# Revit family: Island_LivingDivaniBIM
name_source: partatom
category: Arredi
revit_build: Autodesk Revit 2017 (Build: 20190508_0315(x64)
units: mm (PartAtom-declared; Revit-internal decimal feet)

## family parameters
Basato su piano di lavoro = No
Condiviso = No
Numero OmniClass = 23.40.20.14
Punto di calcolo locali = No
Sempre verticale = Sì
Taglio con vuoti quando caricato = No
Titolo OmniClass = Residential Furniture

## types (4) — shared parameters
Materiale struttura = Metallo LivingDivani 2
Produttore = Living Divani
URL = www.livingdivani.it
zero-valued in all types: Costo

## per-type parameters (varying)
| type | Codice Prodotto | Isalnd160 | Island200 | Modello | Piano in marmo 200 | marmo | piano in marmo 160 |
| Islands 200 | ISLV200 | No | Sì | Islands 200 | No | Marmo | No |
| Islands160 | ISLV160 | Sì | No | Islands 160 | No | <Per categoria> | No |
| Islands 160 + piano in marmo | ISLV160 | Sì | No | Islands 160 | No | Marmo | Sì |
| Islands 200 + piano in marmo | ISLV200 | No | Sì | Islands 200 | Sì | Marmo | No |
